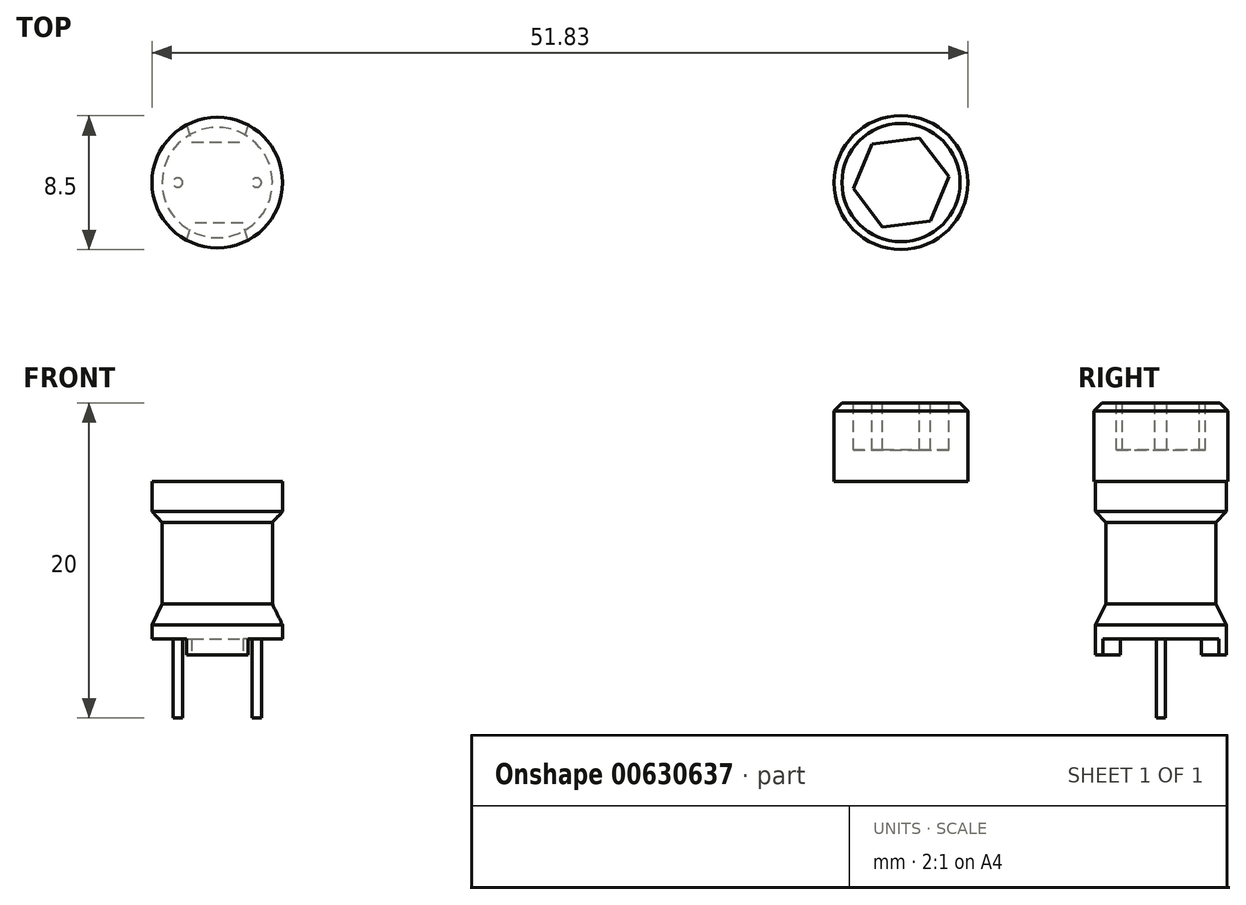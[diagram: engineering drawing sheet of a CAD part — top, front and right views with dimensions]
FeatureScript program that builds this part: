
annotation { "Feature Type Name" : "Feature", "Feature Type Description" : "" }
export const myFeature = defineFeature(function(context is Context, id is Id, definition is map)
    precondition{}
    {
        {
            var Q0;
            Q0=qCreatedBy(makeId("Front.planeOp"),FACE);
            var sketch = newSketch(context, id + "F0", { "sketchPlane" : qUnion([Q0])});
            skLineSegment(sketch, "E0", {"start": v(0, 2.04) * mm, "end": v(0, -13.5) * mm, "construction": true});
            skLineSegment(sketch, "E1", {"start": v(0, 0) * mm, "end": v(4.15, 0) * mm});
            skLineSegment(sketch, "E2", {"start": v(4.15, 0) * mm, "end": v(4.15, -1.9) * mm});
            skLineSegment(sketch, "E3", {"start": v(4.15, -1.9) * mm, "end": v(3.5, -2.58) * mm});
            skLineSegment(sketch, "E4", {"start": v(3.5, -2.58) * mm, "end": v(3.5, -7.78) * mm});
            skLineSegment(sketch, "E5", {"start": v(3.5, -7.78) * mm, "end": v(4.15, -9.1) * mm});
            skLineSegment(sketch, "E6", {"start": v(4.15, -9.1) * mm, "end": v(4.15, -11) * mm});
            skLineSegment(sketch, "E7", {"start": v(4.15, -11) * mm, "end": v(0, -11) * mm});
            skLineSegment(sketch, "E8", {"start": v(0, -11) * mm, "end": v(0, 0) * mm});
            skLineSegment(sketch, "E9", {"start": v(43.43, 23.35) * mm, "end": v(43.43, -29.53) * mm, "construction": true});
            skLineSegment(sketch, "E10.bottom", {"start": v(43.43, 0) * mm, "end": v(47.68, 0) * mm});
            skLineSegment(sketch, "E10.top", {"start": v(43.43, 5) * mm, "end": v(47.68, 5) * mm});
            skLineSegment(sketch, "E10.left", {"start": v(43.43, 0) * mm, "end": v(43.43, 5) * mm});
            skLineSegment(sketch, "E10.right", {"start": v(47.68, 0) * mm, "end": v(47.68, 5) * mm});
            skLineSegment(sketch, "E11.bottom", {"start": v(45.93, 0) * mm, "end": v(43.43, 0) * mm});
            skLineSegment(sketch, "E11.top", {"start": v(45.93, -60) * mm, "end": v(43.43, -60) * mm});
            skLineSegment(sketch, "E11.left", {"start": v(45.93, 0) * mm, "end": v(45.93, -60) * mm});
            skLineSegment(sketch, "E11.right", {"start": v(43.43, 0) * mm, "end": v(43.43, -60) * mm});
            skLineSegment(sketch, "E12.bottom", {"start": v(45.93, -47.5) * mm, "end": v(45.43, -47.5) * mm});
            skLineSegment(sketch, "E12.top", {"start": v(45.93, -60) * mm, "end": v(45.43, -60) * mm});
            skLineSegment(sketch, "E12.left", {"start": v(45.93, -47.5) * mm, "end": v(45.93, -60) * mm});
            skLineSegment(sketch, "E12.right", {"start": v(45.43, -47.5) * mm, "end": v(45.43, -60) * mm});
            skSolve(sketch);
        }
        {
            var Q0;
            Q0=makeQuery(id+"F0.imprint","IMPRINT",FACE,{"disambiguationData":[TD([[makeQuery(id+"F0.imprint","IMPRINT",EDGE,{"derivedFrom":sQuery(id+"F0.wireOp",EDGE,"E1")}),-1.0]])]});
            var Q1;
            Q1=sQuery(id+"F0.wireOp",EDGE,"E0");
            revolve(context, id + "F1", {"surfaceOperationType" : NewSurfaceOperationType.NEW, "entities" : qUnion([Q0]), "axis" : qUnion([Q1]), "revolveType" : RevolveType.FULL});
        }
        {
            var Q0;
            Q0=makeQuery(id+"F1.opRevolve","SWEPT_FACE",FACE,{"disambiguationData":[OSD([sQuery(id+"F0.wireOp",EDGE,"E7")])]});
            var sketch = newSketch(context, id + "F2", { "sketchPlane" : qUnion([Q0])});
            skCircle(sketch, "E13", {"center": v(2.5, 0) * mm, "radius": 0.3 * mm});
            skLineSegment(sketch, "E14", {"start": v(2.5, 0) * mm, "end": v(0, 0) * mm, "construction": true});
            skLineSegment(sketch, "E15", {"start": v(0, 0) * mm, "end": v(-2.5, 0) * mm, "construction": true});
            skCircle(sketch, "E16", {"center": v(-2.5, 0) * mm, "radius": 0.3 * mm});
            skLineSegment(sketch, "E17", {"start": v(-1.94, 3.67) * mm, "end": v(-1.63, 2.58) * mm});
            skLineSegment(sketch, "E18", {"start": v(-1.63, 2.58) * mm, "end": v(0, 2.58) * mm});
            skLineSegment(sketch, "E19", {"start": v(0, 4.98) * mm, "end": v(0, -1.9) * mm, "construction": true});
            skLineSegment(sketch, "E20.MirrorCS", {"start": v(1.94, 3.67) * mm, "end": v(1.63, 2.58) * mm});
            skLineSegment(sketch, "E21.MirrorCS", {"start": v(1.63, 2.58) * mm, "end": v(0, 2.58) * mm});
            skLineSegment(sketch, "E22.MirrorCS", {"start": v(-1.94, -3.67) * mm, "end": v(-1.63, -2.58) * mm});
            skLineSegment(sketch, "E23.MirrorCS", {"start": v(-1.63, -2.58) * mm, "end": v(0, -2.58) * mm});
            skLineSegment(sketch, "E24.MirrorCS", {"start": v(1.63, -2.58) * mm, "end": v(0, -2.58) * mm});
            skLineSegment(sketch, "E25.MirrorCS", {"start": v(1.94, -3.67) * mm, "end": v(1.63, -2.58) * mm});
            skSolve(sketch);
        }
        {
            var Q0;
            Q0=makeQuery(id+"F2.imprint","IMPRINT",FACE,{"disambiguationData":[TD([[makeQuery(id+"F2.imprint","IMPRINT",EDGE,{"derivedFrom":sQuery(id+"F2.wireOp",EDGE,"E16")}),1.0]])]});
            var Q1;
            Q1=makeQuery(id+"F2.imprint","IMPRINT",FACE,{"disambiguationData":[TD([[makeQuery(id+"F2.imprint","IMPRINT",EDGE,{"derivedFrom":sQuery(id+"F2.wireOp",EDGE,"E13")}),1.0]])]});
            extrude(context, id + "F3", {"entities" : qUnion([Q0, Q1]), "operationType" : NewBodyOperationType.ADD, "depth" : 4 * mm, "offsetDistance" : 25 * mm});
        }
        {
            var Q0;
            Q0=makeQuery(id+"F2.imprint","IMPRINT",FACE,{"disambiguationData":[TD([[makeQuery(id+"F2.imprint","IMPRINT",EDGE,{"derivedFrom":sQuery(id+"F2.wireOp",EDGE,"E13")}),-1.0]])]});
            extrude(context, id + "F4", {"entities" : qUnion([Q0]), "operationType" : NewBodyOperationType.REMOVE, "oppositeDirection" : true, "depth" : 1 * mm, "offsetDistance" : 25 * mm});
        }
        {
            var Q0;
            Q0=makeQuery(id+"F0.imprint","IMPRINT",FACE,{"disambiguationData":[TD([[makeQuery(id+"F0.imprint","IMPRINT",EDGE,{"derivedFrom":sQuery(id+"F0.wireOp",EDGE,"E10.bottom")}),1.0]])]});
            var Q1;
            Q1=makeQuery(id+"F0.imprint","IMPRINT",FACE,{"disambiguationData":[TD([[makeQuery(id+"F0.imprint","IMPRINT",EDGE,{"derivedFrom":sQuery(id+"F0.wireOp",EDGE,"E11.bottom")}),1.0]])]});
            var Q2;
            Q2=sQuery(id+"F0.wireOp",EDGE,"E9");
            revolve(context, id + "F5", {"surfaceOperationType" : NewSurfaceOperationType.NEW, "entities" : qUnion([Q0, Q1]), "axis" : qUnion([Q2]), "revolveType" : RevolveType.FULL});
        }
        {
            var Q0;
            Q0=makeQuery(id+"F5.opRevolve","SWEPT_FACE",FACE,{"disambiguationData":[OSD([sQuery(id+"F0.wireOp",EDGE,"E10.top")])]});
            var sketch = newSketch(context, id + "F6", { "sketchPlane" : qUnion([Q0])});
            skCircle(sketch, "E26.cCircle", {"center": v(43.43, 0) * mm, "radius": 2.65 * mm, "construction": true});
            skLineSegment(sketch, "E26.0", {"start": v(44.6, 2.82) * mm, "end": v(46.46, 0.4) * mm});
            skLineSegment(sketch, "E26.1", {"start": v(46.46, 0.4) * mm, "end": v(45.28, -2.43) * mm});
            skLineSegment(sketch, "E26.2", {"start": v(45.28, -2.43) * mm, "end": v(42.25, -2.82) * mm});
            skLineSegment(sketch, "E26.3", {"start": v(42.25, -2.82) * mm, "end": v(40.4, -0.4) * mm});
            skLineSegment(sketch, "E26.4", {"start": v(40.4, -0.4) * mm, "end": v(41.57, 2.43) * mm});
            skLineSegment(sketch, "E26.5", {"start": v(41.57, 2.43) * mm, "end": v(44.6, 2.82) * mm});
            skPoint(sketch, "E26.0.midPoint", {"position": v(45.53, 1.6) * mm});
            skSolve(sketch);
        }
        {
            var Q0;
            Q0 = qSketchRegion(id + "F6", true);
            extrude(context, id + "F7", {"entities" : qUnion([Q0]), "operationType" : NewBodyOperationType.REMOVE, "oppositeDirection" : true, "depth" : 3 * mm, "offsetDistance" : 25 * mm});
        }
        {
            var Q0;
            Q0=makeQuery(id+"F5.opRevolve","SWEPT_EDGE",EDGE,{"disambiguationData":[OSD([sQuery(id+"F0.wireOp",EDGE,"E10.top"),sQuery(id+"F0.wireOp",EDGE,"E10.right")])]});
            var Q1;
            Q1=makeQuery(id+"F5.opRevolve","SWEPT_EDGE",EDGE,{"disambiguationData":[OSD([sQuery(id+"F0.wireOp",EDGE,"E11.top"),sQuery(id+"F0.wireOp",EDGE,"E11.left")])]});
            chamfer(context, id + "F8", {"entities" : qUnion([Q0, Q1]), "width" : .5 * mm, "tangentPropagation" : true});
        }
    });
